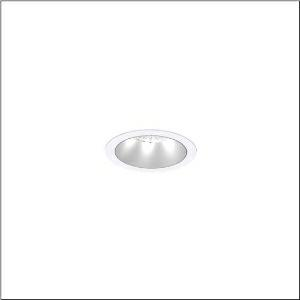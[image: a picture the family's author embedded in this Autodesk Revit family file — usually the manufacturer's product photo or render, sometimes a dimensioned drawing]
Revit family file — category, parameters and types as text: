
# Revit family: lunis_21_m_51db19ec91c
name_source: partatom
category: Lighting Fixtures
units: mm (PartAtom-declared; Revit-internal decimal feet)

## family parameters
Cut with Voids When Loaded = No
Host = Face
Light Source = No
Part Type = Normal
Room Calculation Point = No
Round Connector Dimension = Use Diameter
Shared = No

## types (1)
- --- (1 x LED, 3720 lm, 25.5 W, 6500K)
    Apparent Load = 26 VA
    CIE Flux Codes = 93 99 100 100 100
    Color Rendering = 80
    Color Temperature = 6500K
    Default Elevation = 1800 mm
    Description = Lunis 21 M, downlight, light control with lens, of PMMA, anti glare with reflector, of PC, matt, light emission: direct distribution, LED rated luminous flux: 1.730lm, light colour: 830/840/865, with terminal, 5-pole, mains connection: 220..240V, AC/DC, 0/50..60Hz, housing, round, of diecast aluminium, traffic white (RAL 9016), diameter: 115mm, clamping range: 1..40mm, protection rating (complete): IP20, protection rating (on room side): IP54, insulation class (complete): insulation class II (safety insulation), certification: CE, impact resistance: IK03, packaging unit: 1 piece
    Height = 0 mm  [stored 0 ft]
    Lamp = 1 x LED
    Lamp Light Flux = 3720 lm
    Lamp Power = 25.5 W
    Lamp count = 1
    Length = 115 mm
    Luminous efficacy = 146 lm/W
    Manufacturer = Siteco
    ModVariant = No
    Model = 51DB19EC91C
    Mounting Place = Ceiling
    Mounting Type = Recessed
    Number of Poles = 1
    OnlyDefault = Yes
    Power Factor = 1
    Product Name = Lunis 21 M
    Product group = downlight
    ProductGroupID = 401
    Protection Class = Protection class II
    Protection Degree = IP 20
    RLX_Detail_Level = 1
    RLX_Emergency_Light_Flux = 0 lm
    RLX_Emergency_Type = 0
    RLX_Emergency_Type_DB = No
    RlxData = <blob elided: 14925 chars, md5=17a7a139>
    Socket = socket
    Standby Power = 0 W
    System Light Flux = 3720 lm
    System Power = 26 W
    Type Comments = individual setting: colour temperature 6500K, luminous flux: 100 % | (ON | ON | OFF | OFF) | 700 mA
    Type Image = l_1290856.jpg
    URL = http://relux.com
    VarID = @adj_034877
    Voltage = 0 V
    Weight = 0.00 kg
    Width = 0 mm  [stored 0 ft]

note: [stored X ft] marks values corroborated as IEEE doubles in the binary element streams (Revit-internal decimal feet)

## geometry (parser evidence)
native form markers: Sweep x10
no freeform markers — native parametric forms only
